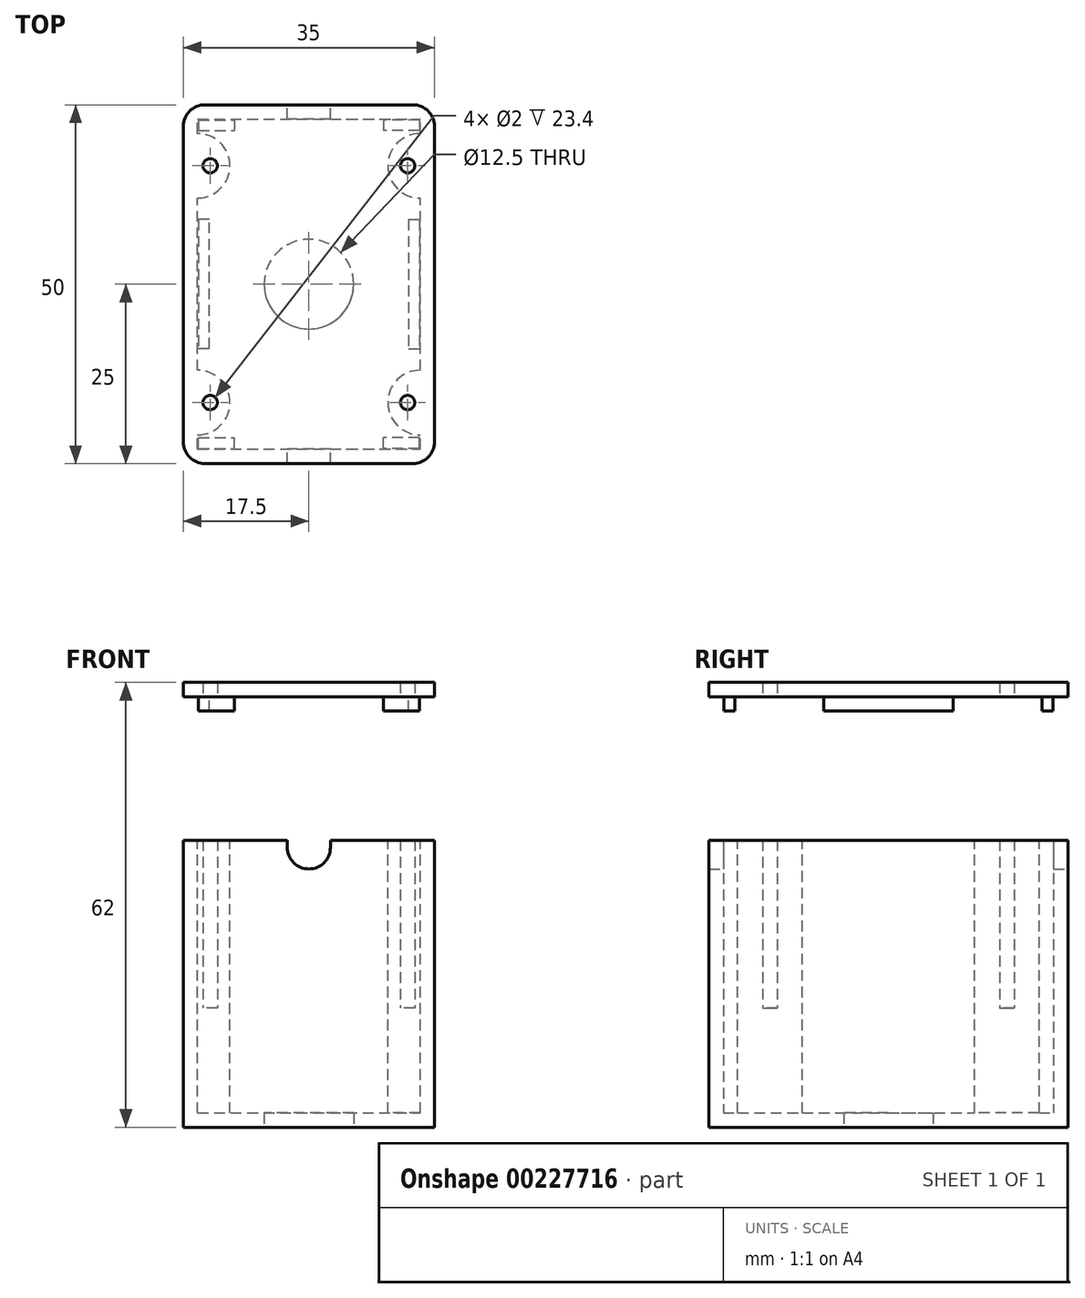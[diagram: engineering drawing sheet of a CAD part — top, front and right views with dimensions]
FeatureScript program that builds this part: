
annotation { "Feature Type Name" : "Feature", "Feature Type Description" : "" }
export const myFeature = defineFeature(function(context is Context, id is Id, definition is map)
    precondition{}
    {
        {
            var Q0;
            Q0=qCreatedBy(makeId("Top.planeOp"),FACE);
            var sketch = newSketch(context, id + "F0", { "sketchPlane" : qUnion([Q0])});
            skLineSegment(sketch, "E0.bottom", {"start": v(0, 0) * mm, "end": v(35, 0) * mm});
            skLineSegment(sketch, "E0.top", {"start": v(0, 50) * mm, "end": v(35, 50) * mm});
            skLineSegment(sketch, "E0.left", {"start": v(0, 0) * mm, "end": v(0, 50) * mm});
            skLineSegment(sketch, "E0.right", {"start": v(35, 0) * mm, "end": v(35, 50) * mm});
            skSolve(sketch);
        }
        {
            var Q0;
            Q0 = qSketchRegion(id + "F0", true);
            extrude(context, id + "F1", {"entities" : qUnion([Q0]), "depth" : 40 * mm});
        }
        {
            var Q0;
            Q0=makeQuery(id+"F1.opExtrude","CAP_FACE",FACE,{"disambiguationData":[OSD([sQuery(id+"F0.wireOp",EDGE,"E0.bottom"),sQuery(id+"F0.wireOp",EDGE,"E0.top"),sQuery(id+"F0.wireOp",EDGE,"E0.left"),sQuery(id+"F0.wireOp",EDGE,"E0.right")])],"isStart":false});
            shell(context, id + "F2", {"entities" : qUnion([Q0]), "thickness" : 2 * mm});
        }
        {
            var Q0;
            Q0=makeQuery(id+"F1.opExtrude","CAP_FACE",FACE,{"disambiguationData":[OSD([sQuery(id+"F0.wireOp",EDGE,"E0.bottom"),sQuery(id+"F0.wireOp",EDGE,"E0.top"),sQuery(id+"F0.wireOp",EDGE,"E0.left"),sQuery(id+"F0.wireOp",EDGE,"E0.right")])],"isStart":true});
            var sketch = newSketch(context, id + "F3", { "sketchPlane" : qUnion([Q0])});
            skCircle(sketch, "E1", {"center": v(17.5, -25) * mm, "radius": 6.25 * mm});
            skSolve(sketch);
        }
        {
            var Q0;
            Q0 = qSketchRegion(id + "F3", true);
            extrude(context, id + "F4", {"entities" : qUnion([Q0]), "operationType" : NewBodyOperationType.REMOVE, "endBound" : BoundingType.UP_TO_NEXT, "oppositeDirection" : true, "depth" : 25 * mm});
        }
        {
            var Q0;
            Q0=makeQuery(id+"F1.opExtrude","SWEPT_FACE",FACE,{"disambiguationData":[OSD([sQuery(id+"F0.wireOp",EDGE,"E0.top")])]});
            var sketch = newSketch(context, id + "F5", { "sketchPlane" : qUnion([Q0])});
            skLineSegment(sketch, "E2", {"start": v(-20.5, 40) * mm, "end": v(-20.5, 39) * mm});
            skLineSegment(sketch, "E3", {"start": v(-14.5, 40) * mm, "end": v(-14.5, 39) * mm});
            skArc(sketch, "E4", {"start": v(-20.5, 39) * mm, "mid": v(-17.5, 36) * mm, "end": v(-14.5, 39) * mm});
            skSolve(sketch);
        }
        {
            var Q0;
            Q0 = qSketchRegion(id + "F5", true);
            var Q1;
            {var subQ0=sQuery(id+"F5.wireOp",EDGE,"E2");Q1=makeQuery(id+"F5.imprint","IMPRINT",FACE,{"disambiguationData":[TD([[makeQuery(id+"F5.imprint","IMPRINT",EDGE,{"derivedFrom":subQ0}),1.0]])]});}
            extrude(context, id + "F6", {"entities" : qUnion([Q0, Q1]), "operationType" : NewBodyOperationType.REMOVE, "endBound" : BoundingType.THROUGH_ALL, "oppositeDirection" : true, "depth" : 25 * mm});
        }
        {
            var Q0;
            {var subQ0=sQuery(id+"F0.wireOp",EDGE,"E0.bottom");var subQ1=sQuery(id+"F0.wireOp",EDGE,"E0.left");var subQ2=sQuery(id+"F0.wireOp",EDGE,"E0.top");Q0=makeQuery(id+"F6.boolean.opBoolean","SPLIT",FACE,{"disambiguationData":[TD([makeQuery(id+"F1.opExtrude","SWEPT_FACE",FACE,{"disambiguationData":[OSD([subQ1])]})])],"derivedFrom":makeQuery(id+"F1.opExtrude","CAP_FACE",FACE,{"disambiguationData":[OSD([subQ0,subQ2,subQ1,sQuery(id+"F0.wireOp",EDGE,"E0.right")])],"isStart":false})});}
            var sketch = newSketch(context, id + "F7", { "sketchPlane" : qUnion([Q0])});
            skArc(sketch, "E5", {"start": v(2, 37) * mm, "mid": v(6.5, 41.5) * mm, "end": v(2, 46) * mm});
            skArc(sketch, "E6.MirrorCS", {"start": v(33, 37) * mm, "mid": v(28.5, 41.5) * mm, "end": v(33, 46) * mm});
            skArc(sketch, "E7.MirrorCS", {"start": v(33, 13) * mm, "mid": v(28.5, 8.5) * mm, "end": v(33, 4) * mm});
            skArc(sketch, "E8.MirrorCS", {"start": v(2, 13) * mm, "mid": v(6.5, 8.5) * mm, "end": v(2, 4) * mm});
            skLineSegment(sketch, "E9", {"start": v(2, 46) * mm, "end": v(2, 37) * mm});
            skLineSegment(sketch, "E10", {"start": v(33, 46) * mm, "end": v(33, 37) * mm});
            skLineSegment(sketch, "E11", {"start": v(33, 13) * mm, "end": v(33, 4) * mm});
            skLineSegment(sketch, "E12", {"start": v(2, 13) * mm, "end": v(2, 4) * mm});
            skSolve(sketch);
        }
        {
            var Q0;
            Q0 = qSketchRegion(id + "F7", true);
            extrude(context, id + "F8", {"entities" : qUnion([Q0]), "operationType" : NewBodyOperationType.ADD, "oppositeDirection" : true, "depth" : 39 * mm});
        }
        {
            var Q0;
            {var subQ0=sQuery(id+"F0.wireOp",EDGE,"E0.bottom");var subQ1=sQuery(id+"F0.wireOp",EDGE,"E0.right");var subQ2=sQuery(id+"F0.wireOp",EDGE,"E0.top");Q0=makeQuery(id+"F8.boolean.opBoolean","MERGE",FACE,{"derivedFrom":[makeQuery(id+"F6.boolean.opBoolean","SPLIT",FACE,{"disambiguationData":[TD([makeQuery(id+"F1.opExtrude","SWEPT_FACE",FACE,{"disambiguationData":[OSD([subQ1])]})])],"derivedFrom":makeQuery(id+"F1.opExtrude","CAP_FACE",FACE,{"disambiguationData":[OSD([subQ0,subQ2,sQuery(id+"F0.wireOp",EDGE,"E0.left"),subQ1])],"isStart":false})}),makeQuery(id+"F8.opExtrude","CAP_FACE",FACE,{"disambiguationData":[OSD([sQuery(id+"F7.wireOp",EDGE,"E6.MirrorCS"),sQuery(id+"F7.wireOp",EDGE,"E10")])],"isStart":true}),makeQuery(id+"F8.opExtrude","CAP_FACE",FACE,{"disambiguationData":[OSD([sQuery(id+"F7.wireOp",EDGE,"E7.MirrorCS"),sQuery(id+"F7.wireOp",EDGE,"E11")])],"isStart":true})]});}
            cPlane(context, id + "F9", {"entities" : qUnion([Q0]), "cplaneType" : CPlaneType.OFFSET, "offset" : 20 * mm, "width" : 150 * mm, "height" : 150 * mm});
        }
        {
            var Q0;
            Q0=qCreatedBy(id+"F9.planeOp",FACE);
            var sketch = newSketch(context, id + "F10", { "sketchPlane" : qUnion([Q0])});
            skLineSegment(sketch, "E13.bottom", {"start": v(0, 0) * mm, "end": v(35, 0) * mm});
            skLineSegment(sketch, "E13.top", {"start": v(0, 50) * mm, "end": v(35, 50) * mm});
            skLineSegment(sketch, "E13.left", {"start": v(0, 0) * mm, "end": v(0, 50) * mm});
            skLineSegment(sketch, "E13.right", {"start": v(35, 0) * mm, "end": v(35, 50) * mm});
            skSolve(sketch);
        }
        {
            var Q0;
            Q0 = qSketchRegion(id + "F10", true);
            extrude(context, id + "F11", {"entities" : qUnion([Q0]), "depth" : 2 * mm});
        }
        {
            var Q0;
            Q0=makeQuery(id+"F11.opExtrude","CAP_FACE",FACE,{"disambiguationData":[OSD([sQuery(id+"F10.wireOp",EDGE,"E13.bottom"),sQuery(id+"F10.wireOp",EDGE,"E13.top"),sQuery(id+"F10.wireOp",EDGE,"E13.left"),sQuery(id+"F10.wireOp",EDGE,"E13.right")])],"isStart":false});
            var sketch = newSketch(context, id + "F12", { "sketchPlane" : qUnion([Q0])});
            skLineSegment(sketch, "E14.bottom", {"start": v(3.6, 34) * mm, "end": v(2.1, 34) * mm});
            skLineSegment(sketch, "E14.left", {"start": v(3.6, 34) * mm, "end": v(3.6, 25) * mm});
            skLineSegment(sketch, "E14.right", {"start": v(2.1, 34) * mm, "end": v(2.1, 25) * mm});
            skLineSegment(sketch, "E15.bottom", {"start": v(2.1, 47.9) * mm, "end": v(7.1, 47.9) * mm});
            skLineSegment(sketch, "E15.top", {"start": v(2.1, 46.4) * mm, "end": v(7.1, 46.4) * mm});
            skLineSegment(sketch, "E15.left", {"start": v(2.1, 47.9) * mm, "end": v(2.1, 46.4) * mm});
            skLineSegment(sketch, "E15.right", {"start": v(7.1, 47.9) * mm, "end": v(7.1, 46.4) * mm});
            skLineSegment(sketch, "E16.MirrorCS", {"start": v(32.9, 47.9) * mm, "end": v(32.9, 46.4) * mm});
            skLineSegment(sketch, "E17.MirrorCS", {"start": v(27.9, 47.9) * mm, "end": v(27.9, 46.4) * mm});
            skLineSegment(sketch, "E18.MirrorCS", {"start": v(31.4, 34) * mm, "end": v(32.9, 34) * mm});
            skLineSegment(sketch, "E19.MirrorCS", {"start": v(31.4, 34) * mm, "end": v(31.4, 25) * mm});
            skLineSegment(sketch, "E20.MirrorCS", {"start": v(32.9, 47.9) * mm, "end": v(27.9, 47.9) * mm});
            skLineSegment(sketch, "E21.MirrorCS", {"start": v(32.9, 46.4) * mm, "end": v(27.9, 46.4) * mm});
            skLineSegment(sketch, "E22.MirrorCS", {"start": v(32.9, 34) * mm, "end": v(32.9, 25) * mm});
            skLineSegment(sketch, "E23.MirrorCS", {"start": v(3.6, 16) * mm, "end": v(2.1, 16) * mm});
            skLineSegment(sketch, "E24.MirrorCS", {"start": v(32.9, 2.1) * mm, "end": v(32.9, 3.6) * mm});
            skLineSegment(sketch, "E25.MirrorCS", {"start": v(7.1, 2.1) * mm, "end": v(7.1, 3.6) * mm});
            skLineSegment(sketch, "E26.MirrorCS", {"start": v(31.4, 16) * mm, "end": v(32.9, 16) * mm});
            skLineSegment(sketch, "E27.MirrorCS", {"start": v(27.9, 2.1) * mm, "end": v(27.9, 3.6) * mm});
            skLineSegment(sketch, "E28.MirrorCS", {"start": v(2.1, 2.1) * mm, "end": v(2.1, 3.6) * mm});
            skLineSegment(sketch, "E29.MirrorCS", {"start": v(2.1, 3.6) * mm, "end": v(7.1, 3.6) * mm});
            skLineSegment(sketch, "E30.MirrorCS", {"start": v(2.1, 2.1) * mm, "end": v(7.1, 2.1) * mm});
            skLineSegment(sketch, "E31.MirrorCS", {"start": v(2.1, 16) * mm, "end": v(2.1, 25) * mm});
            skLineSegment(sketch, "E32.MirrorCS", {"start": v(3.6, 16) * mm, "end": v(3.6, 25) * mm});
            skLineSegment(sketch, "E33.MirrorCS", {"start": v(32.9, 3.6) * mm, "end": v(27.9, 3.6) * mm});
            skLineSegment(sketch, "E34.MirrorCS", {"start": v(32.9, 2.1) * mm, "end": v(27.9, 2.1) * mm});
            skLineSegment(sketch, "E35.MirrorCS", {"start": v(32.9, 16) * mm, "end": v(32.9, 25) * mm});
            skLineSegment(sketch, "E36.MirrorCS", {"start": v(31.4, 16) * mm, "end": v(31.4, 25) * mm});
            skSolve(sketch);
        }
        {
            var Q0;
            Q0 = qSketchRegion(id + "F12", true);
            extrude(context, id + "F13", {"entities" : qUnion([Q0]), "operationType" : NewBodyOperationType.ADD, "oppositeDirection" : true, "depth" : 4 * mm});
        }
        {
            var Q0;
            {var subQ0=sQuery(id+"F0.wireOp",EDGE,"E0.bottom");var subQ1=sQuery(id+"F0.wireOp",EDGE,"E0.right");var subQ2=sQuery(id+"F0.wireOp",EDGE,"E0.top");Q0=makeQuery(id+"F8.boolean.opBoolean","MERGE",FACE,{"derivedFrom":[makeQuery(id+"F6.boolean.opBoolean","SPLIT",FACE,{"disambiguationData":[TD([makeQuery(id+"F1.opExtrude","SWEPT_FACE",FACE,{"disambiguationData":[OSD([subQ1])]})])],"derivedFrom":makeQuery(id+"F1.opExtrude","CAP_FACE",FACE,{"disambiguationData":[OSD([subQ0,subQ2,sQuery(id+"F0.wireOp",EDGE,"E0.left"),subQ1])],"isStart":false})}),makeQuery(id+"F8.opExtrude","CAP_FACE",FACE,{"disambiguationData":[OSD([sQuery(id+"F7.wireOp",EDGE,"E6.MirrorCS"),sQuery(id+"F7.wireOp",EDGE,"E10")])],"isStart":true}),makeQuery(id+"F8.opExtrude","CAP_FACE",FACE,{"disambiguationData":[OSD([sQuery(id+"F7.wireOp",EDGE,"E7.MirrorCS"),sQuery(id+"F7.wireOp",EDGE,"E11")])],"isStart":true})]});}
            var sketch = newSketch(context, id + "F14", { "sketchPlane" : qUnion([Q0])});
            skCircle(sketch, "E37", {"center": v(31.25, 41.5) * mm, "radius": 1 * mm});
            skLineSegment(sketch, "E38", {"start": v(35, 25) * mm, "end": v(30.73, 25) * mm});
            skLineSegment(sketch, "E39", {"start": v(17.5, 0) * mm, "end": v(17.5, 5.89) * mm});
            skCircle(sketch, "E40.MirrorC", {"center": v(31.25, 8.5) * mm, "radius": 1 * mm});
            skCircle(sketch, "E41.MirrorC", {"center": v(3.75, 41.5) * mm, "radius": 1 * mm});
            skCircle(sketch, "E42.MirrorC", {"center": v(3.75, 8.5) * mm, "radius": 1 * mm});
            skSolve(sketch);
        }
        {
            var Q0;
            Q0 = qSketchRegion(id + "F14", true);
            extrude(context, id + "F15", {"entities" : qUnion([Q0]), "operationType" : NewBodyOperationType.REMOVE, "endBound" : BoundingType.SYMMETRIC, "depth" : 46.8 * mm});
        }
        {
            var Q0;
            Q0=makeQuery(id+"F1.opExtrude","SWEPT_EDGE",EDGE,{"disambiguationData":[OSD([sQuery(id+"F0.wireOp",EDGE,"E0.bottom"),sQuery(id+"F0.wireOp",EDGE,"E0.right")])]});
            var Q1;
            Q1=makeQuery(id+"F1.opExtrude","SWEPT_EDGE",EDGE,{"disambiguationData":[OSD([sQuery(id+"F0.wireOp",EDGE,"E0.bottom"),sQuery(id+"F0.wireOp",EDGE,"E0.left")])]});
            var Q2;
            Q2=makeQuery(id+"F1.opExtrude","SWEPT_EDGE",EDGE,{"disambiguationData":[OSD([sQuery(id+"F0.wireOp",EDGE,"E0.top"),sQuery(id+"F0.wireOp",EDGE,"E0.right")])]});
            var Q3;
            Q3=makeQuery(id+"F1.opExtrude","SWEPT_EDGE",EDGE,{"disambiguationData":[OSD([sQuery(id+"F0.wireOp",EDGE,"E0.top"),sQuery(id+"F0.wireOp",EDGE,"E0.left")])]});
            var Q4;
            Q4=makeQuery(id+"F11.opExtrude","SWEPT_EDGE",EDGE,{"disambiguationData":[OSD([sQuery(id+"F10.wireOp",EDGE,"E13.bottom"),sQuery(id+"F10.wireOp",EDGE,"E13.left")])]});
            var Q5;
            Q5=makeQuery(id+"F11.opExtrude","SWEPT_EDGE",EDGE,{"disambiguationData":[OSD([sQuery(id+"F10.wireOp",EDGE,"E13.bottom"),sQuery(id+"F10.wireOp",EDGE,"E13.right")])]});
            var Q6;
            Q6=makeQuery(id+"F11.opExtrude","SWEPT_EDGE",EDGE,{"disambiguationData":[OSD([sQuery(id+"F10.wireOp",EDGE,"E13.top"),sQuery(id+"F10.wireOp",EDGE,"E13.right")])]});
            var Q7;
            Q7=makeQuery(id+"F11.opExtrude","SWEPT_EDGE",EDGE,{"disambiguationData":[OSD([sQuery(id+"F10.wireOp",EDGE,"E13.top"),sQuery(id+"F10.wireOp",EDGE,"E13.left")])]});
            fillet(context, id + "F16", {"entities" : qUnion([Q0, Q1, Q2, Q3, Q4, Q5, Q6, Q7]), "radius" : 3 * mm, "tangentPropagation" : true, "allowEdgeOverflow" : false});
        }
    });
